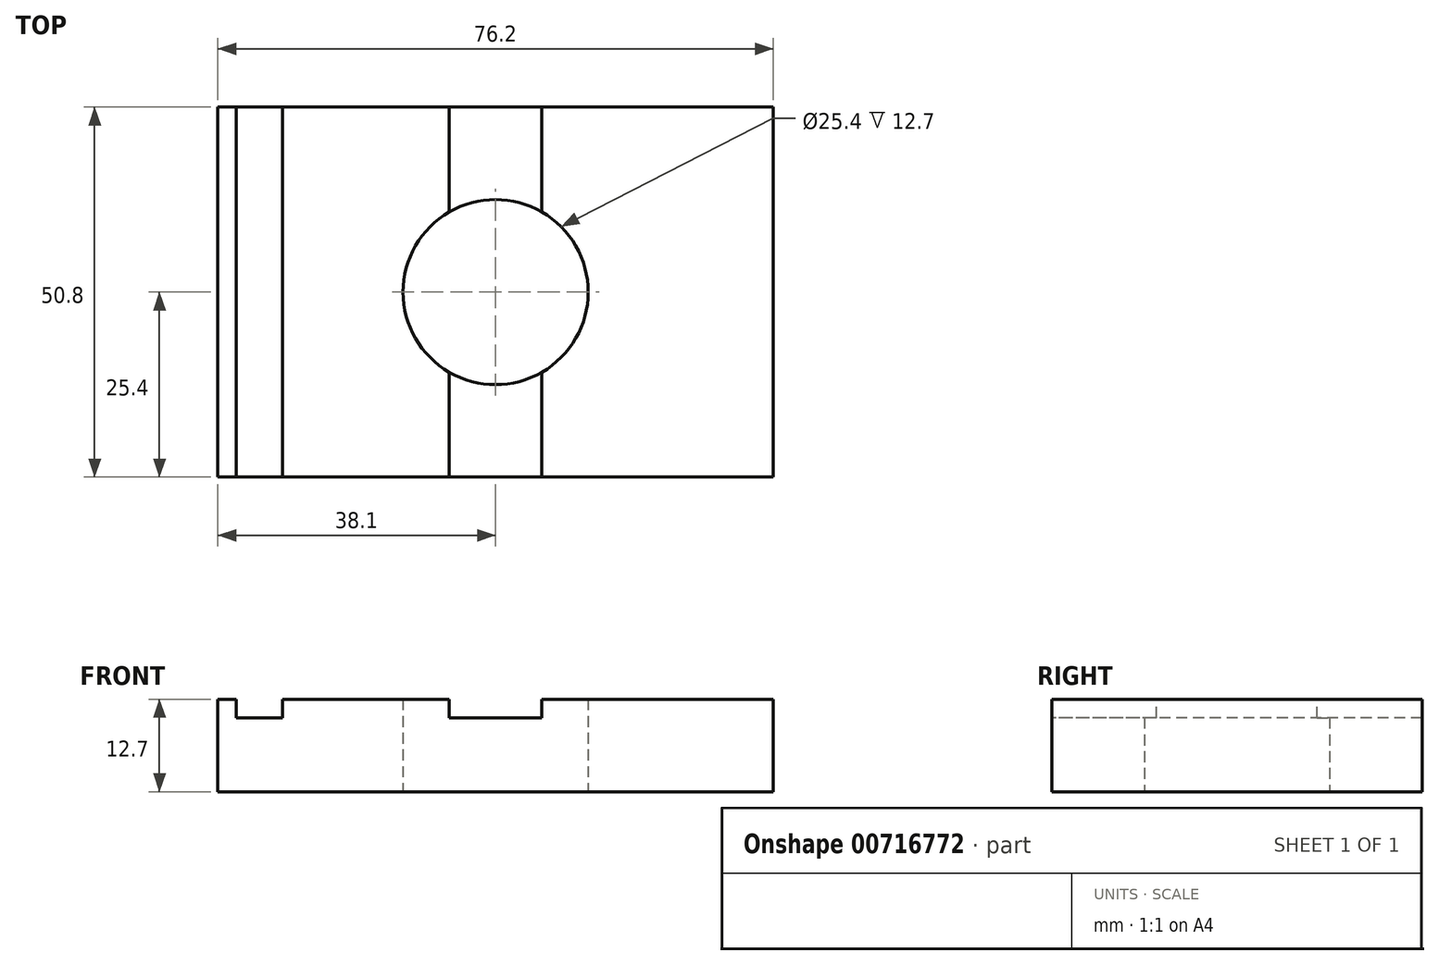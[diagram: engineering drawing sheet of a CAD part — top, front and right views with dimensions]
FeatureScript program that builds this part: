
annotation { "Feature Type Name" : "Feature", "Feature Type Description" : "" }
export const myFeature = defineFeature(function(context is Context, id is Id, definition is map)
    precondition{}
    {
        {
            var Q0;
            Q0=qCreatedBy(makeId("Top.planeOp"),FACE);
            var sketch = newSketch(context, id + "F0", { "sketchPlane" : qUnion([Q0])});
            skLineSegment(sketch, "E0.bottom", {"start": v(38.1, 25.4) * mm, "end": v(-38.1, 25.4) * mm});
            skLineSegment(sketch, "E0.top", {"start": v(38.1, -25.4) * mm, "end": v(-38.1, -25.4) * mm});
            skLineSegment(sketch, "E0.left", {"start": v(38.1, 25.4) * mm, "end": v(38.1, -25.4) * mm});
            skLineSegment(sketch, "E0.right", {"start": v(-38.1, 25.4) * mm, "end": v(-38.1, -25.4) * mm});
            skPoint(sketch, "E0.middle", {"position": v(0, 0) * mm});
            skCircle(sketch, "E1", {"center": v(0, 0) * mm, "radius": 12.7 * mm});
            skSolve(sketch);
        }
        {
            var Q0;
            Q0=makeQuery(id+"F0.imprint","IMPRINT",FACE,{"disambiguationData":[TD([[makeQuery(id+"F0.imprint","IMPRINT",EDGE,{"derivedFrom":sQuery(id+"F0.wireOp",EDGE,"E0.bottom")}),1.0]])]});
            extrude(context, id + "F1", {"entities" : qUnion([Q0]), "depth" : 12.7 * mm, "offsetDistance" : 25.4 * mm});
        }
        {
            var Q0;
            Q0=makeQuery(id+"F1.opExtrude","CAP_FACE",FACE,{"disambiguationData":[OSD([sQuery(id+"F0.wireOp",EDGE,"E0.bottom"),sQuery(id+"F0.wireOp",EDGE,"E0.top"),sQuery(id+"F0.wireOp",EDGE,"E0.left"),sQuery(id+"F0.wireOp",EDGE,"E0.right"),sQuery(id+"F0.wireOp",EDGE,"E1")])],"isStart":false});
            var sketch = newSketch(context, id + "F2", { "sketchPlane" : qUnion([Q0])});
            skLineSegment(sketch, "E2.bottom", {"start": v(-35.56, 25.4) * mm, "end": v(-29.21, 25.4) * mm});
            skLineSegment(sketch, "E2.top", {"start": v(-35.56, -25.4) * mm, "end": v(-29.21, -25.4) * mm});
            skLineSegment(sketch, "E2.left", {"start": v(-35.56, 25.4) * mm, "end": v(-35.56, -25.4) * mm});
            skLineSegment(sketch, "E2.right", {"start": v(-29.21, 25.4) * mm, "end": v(-29.21, -25.4) * mm});
            skLineSegment(sketch, "E3", {"start": v(-6.35, 25.4) * mm, "end": v(-6.35, -25.4) * mm});
            skLineSegment(sketch, "E4", {"start": v(-6.35, -25.4) * mm, "end": v(6.35, -25.4) * mm});
            skLineSegment(sketch, "E5", {"start": v(6.35, -25.4) * mm, "end": v(6.35, 25.4) * mm});
            skLineSegment(sketch, "E6", {"start": v(6.35, 25.4) * mm, "end": v(-6.35, 25.4) * mm});
            skPoint(sketch, "E7", {"position": v(0, 0) * mm});
            skLineSegment(sketch, "E8", {"start": v(0, 25.4) * mm, "end": v(0, -25.4) * mm, "construction": true});
            skSolve(sketch);
        }
        {
            var Q0;
            Q0=makeQuery(id+"F2.imprint","IMPRINT",FACE,{"disambiguationData":[TD([[makeQuery(id+"F2.imprint","IMPRINT",EDGE,{"derivedFrom":sQuery(id+"F2.wireOp",EDGE,"E2.bottom")}),1.0]])]});
            var Q1;
            {var subQ0=sQuery(id+"F2.wireOp",EDGE,"E4");Q1=makeQuery(id+"F2.imprint","IMPRINT",FACE,{"disambiguationData":[TD([[makeQuery(id+"F2.imprint","IMPRINT",EDGE,{"derivedFrom":subQ0}),-1.0]])]});}
            var Q2;
            {var subQ0=sQuery(id+"F2.wireOp",EDGE,"E6");Q2=makeQuery(id+"F2.imprint","IMPRINT",FACE,{"disambiguationData":[TD([[makeQuery(id+"F2.imprint","IMPRINT",EDGE,{"derivedFrom":subQ0}),1.0]])]});}
            extrude(context, id + "F3", {"entities" : qUnion([Q0, Q1, Q2]), "operationType" : NewBodyOperationType.REMOVE, "oppositeDirection" : true, "depth" : 2.54 * mm, "offsetDistance" : 25.4 * mm});
        }
    });
